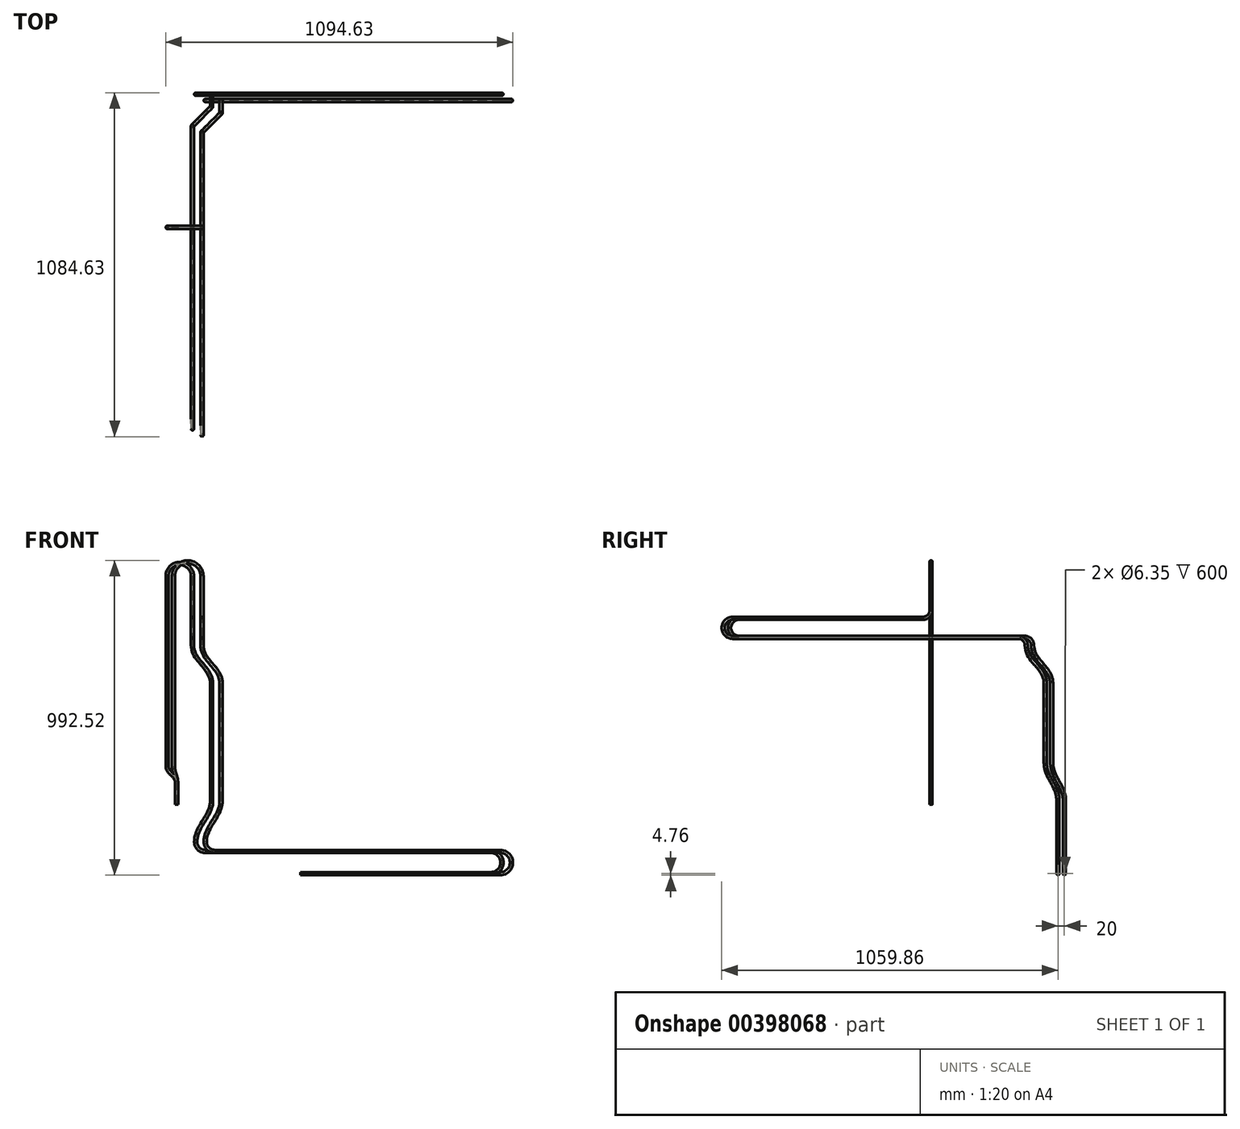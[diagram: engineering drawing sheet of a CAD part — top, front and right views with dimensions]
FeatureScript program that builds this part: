
annotation { "Feature Type Name" : "Feature", "Feature Type Description" : "" }
export const myFeature = defineFeature(function(context is Context, id is Id, definition is map)
    precondition{}
    {
        {
            var Q0;
            Q0=qCreatedBy(makeId("Top.planeOp"),FACE);
            var sketch = newSketch(context, id + "F0", { "sketchPlane" : qUnion([Q0])});
            skCircle(sketch, "E0", {"center": v(0, 0) * mm, "radius": 4.76 * mm});
            skCircle(sketch, "E1", {"center": v(0, 0) * mm, "radius": 3.17 * mm});
            skSolve(sketch);
        }
        {
            var Q0;
            Q0=qCreatedBy(makeId("Front.planeOp"),FACE);
            var sketch = newSketch(context, id + "F1", { "sketchPlane" : qUnion([Q0])});
            skLineSegment(sketch, "E2", {"start": v(80, 612) * mm, "end": v(80, 720) * mm});
            skArc(sketch, "E3", {"start": v(80, 720) * mm, "mid": v(35, 765) * mm, "end": v(-10, 720) * mm});
            skLineSegment(sketch, "E4", {"start": v(0, 70) * mm, "end": v(0, 0) * mm});
            skFitSpline(sketch, "E5", {"points": [v(0, 70) * mm, v(-5, 95) * mm, v(-10, 120) * mm], "startDerivative": vector(0, 60) * mm, "endDerivative": vector(0, 60) * mm});
            skLineSegment(sketch, "E6", {"start": v(-10, 110) * mm, "end": v(-10, 120) * mm, "construction": true});
            skLineSegment(sketch, "E7", {"start": v(0, 80) * mm, "end": v(0, 70) * mm, "construction": true});
            skLineSegment(sketch, "E8", {"start": v(0, 70) * mm, "end": v(-10, 120) * mm, "construction": true});
            skLineSegment(sketch, "E9", {"start": v(-10, 120) * mm, "end": v(-10, 720) * mm});
            skSolve(sketch);
        }
        {
            var Q0;
            Q0=qCreatedBy(makeId("Right.planeOp"),FACE);
            var Q1;
            Q1=sQuery(id+"F1.wireOp",VERTEX,"E2.start");
            cPlane(context, id + "F2", {"entities" : qUnion([Q0, Q1]), "cplaneType" : CPlaneType.PLANE_POINT, "offset" : 25 * mm, "width" : 150 * mm, "height" : 150 * mm});
        }
        {
            var Q0;
            Q0=qCreatedBy(id+"F2.planeOp",FACE);
            var sketch = newSketch(context, id + "F3", { "sketchPlane" : qUnion([Q0])});
            skArc(sketch, "E10.MirrorCS", {"start": v(0, 612) * mm, "mid": v(-7.32, 594.32) * mm, "end": v(-25, 587) * mm});
            skArc(sketch, "E11.MirrorCS", {"start": v(275, 527) * mm, "mid": v(292.68, 519.68) * mm, "end": v(300, 502) * mm});
            skLineSegment(sketch, "E12.MirrorCS", {"start": v(300, 502) * mm, "end": v(300, 517.1) * mm, "construction": true});
            skLineSegment(sketch, "E13.MirrorCS", {"start": v(-25, 587) * mm, "end": v(-625, 587) * mm});
            skArc(sketch, "E14.MirrorCS", {"start": v(-625, 527) * mm, "mid": v(-655, 557) * mm, "end": v(-625, 587) * mm});
            skLineSegment(sketch, "E15.MirrorCS", {"start": v(-625, 527) * mm, "end": v(275, 527) * mm});
            skSolve(sketch);
        }
        {
            var Q0;
            Q0=sQuery(id+"F3.wireOp",EDGE,"E12.MirrorCS");
            cPlane(context, id + "F4", {"entities" : qUnion([Q0]), "cplaneType" : CPlaneType.LINE_ANGLE, "offset" : 25 * mm, "angle" : 45 * degree, "oppositeDirection" : true, "width" : 150 * mm, "height" : 150 * mm});
        }
        {
            var Q0;
            Q0=qCreatedBy(id+"F4.planeOp",FACE);
            var sketch = newSketch(context, id + "F5", { "sketchPlane" : qUnion([Q0])});
            skFitSpline(sketch, "E16", {"points": [v(268.7, 502) * mm, v(311.2, 442) * mm, v(353.7, 382) * mm], "startDerivative": vector(0, -150) * mm, "endDerivative": vector(0, -150) * mm});
            skLineSegment(sketch, "E17", {"start": v(268.7, 477) * mm, "end": v(268.7, 502) * mm, "construction": true});
            skLineSegment(sketch, "E18", {"start": v(353.7, 407) * mm, "end": v(353.7, 382) * mm, "construction": true});
            skLineSegment(sketch, "E19", {"start": v(353.7, 382) * mm, "end": v(268.7, 502) * mm, "construction": true});
            skLineSegment(sketch, "E20", {"start": v(353.7, 382) * mm, "end": v(353.7, 132) * mm});
            skSolve(sketch);
        }
        {
            var Q0;
            Q0=qCreatedBy(makeId("Right.planeOp"),FACE);
            var Q1;
            Q1=sQuery(id+"F5.wireOp",VERTEX,"E20.end");
            cPlane(context, id + "F6", {"entities" : qUnion([Q0, Q1]), "cplaneType" : CPlaneType.PLANE_POINT, "offset" : 25 * mm, "width" : 150 * mm, "height" : 150 * mm});
        }
        {
            var Q0;
            Q0=qCreatedBy(id+"F6.planeOp",FACE);
            var sketch = newSketch(context, id + "F7", { "sketchPlane" : qUnion([Q0])});
            skFitSpline(sketch, "E21", {"points": [v(360.1, 132) * mm, v(380.1, 72) * mm, v(400.1, 12) * mm], "startDerivative": vector(0, -150) * mm, "endDerivative": vector(0, -150) * mm});
            skLineSegment(sketch, "E22", {"start": v(360.1, 132) * mm, "end": v(360.1, 107) * mm, "construction": true});
            skLineSegment(sketch, "E23", {"start": v(400.1, 37) * mm, "end": v(400.1, 12) * mm, "construction": true});
            skLineSegment(sketch, "E24", {"start": v(400.1, 12) * mm, "end": v(360.1, 132) * mm, "construction": true});
            skSolve(sketch);
        }
        {
            var Q0;
            Q0=sQuery(id+"F7.wireOp",VERTEX,"E21.end");
            var Q1;
            Q1=qCreatedBy(makeId("Front.planeOp"),FACE);
            cPlane(context, id + "F8", {"entities" : qUnion([Q0, Q1]), "cplaneType" : CPlaneType.PLANE_POINT, "offset" : 25 * mm, "width" : 150 * mm, "height" : 150 * mm});
        }
        {
            var Q0;
            Q0=qCreatedBy(id+"F8.planeOp",FACE);
            var sketch = newSketch(context, id + "F9", { "sketchPlane" : qUnion([Q0])});
            skFitSpline(sketch, "E25", {"points": [v(140.1, 12) * mm, v(115.1, -53) * mm, v(90.1, -118) * mm], "startDerivative": vector(0, -150) * mm, "endDerivative": vector(0, -150) * mm});
            skLineSegment(sketch, "E26", {"start": v(140.1, 12) * mm, "end": v(140.1, -13) * mm, "construction": true});
            skLineSegment(sketch, "E27", {"start": v(90.1, -93) * mm, "end": v(90.1, -118) * mm, "construction": true});
            skLineSegment(sketch, "E28", {"start": v(90.1, -118) * mm, "end": v(140.1, 12) * mm, "construction": true});
            skArc(sketch, "E29", {"start": v(90.1, -118) * mm, "mid": v(98.9, -139.21) * mm, "end": v(120.1, -148) * mm});
            skLineSegment(sketch, "E30", {"start": v(120.1, -148) * mm, "end": v(1020.1, -148) * mm});
            skArc(sketch, "E31", {"start": v(1020.1, -218) * mm, "mid": v(1055.1, -183) * mm, "end": v(1020.1, -148) * mm});
            skLineSegment(sketch, "E32", {"start": v(1020.1, -218) * mm, "end": v(420.1, -218) * mm});
            skSolve(sketch);
        }
        {
            var Q0;
            Q0=qSketchRegion(id+"F0",true);
            var Q1;
            Q1=qConstructionFilter(qBodyType(qCreatedBy(id+"F1",EDGE),BodyType.WIRE),ConstructionObject.NO);
            var Q2;
            Q2=qConstructionFilter(qBodyType(qCreatedBy(id+"F3",EDGE),BodyType.WIRE),ConstructionObject.NO);
            var Q3;
            Q3=qConstructionFilter(qBodyType(qCreatedBy(id+"F5",EDGE),BodyType.WIRE),ConstructionObject.NO);
            var Q4;
            Q4=qConstructionFilter(qBodyType(qCreatedBy(id+"F7",EDGE),BodyType.WIRE),ConstructionObject.NO);
            var Q5;
            Q5=qConstructionFilter(qBodyType(qCreatedBy(id+"F9",EDGE),BodyType.WIRE),ConstructionObject.NO);
            sweep(context, id + "F10", {"profiles" : qUnion([Q0]), "path" : qUnion([Q1, Q2, Q3, Q4, Q5])});
        }
        {
            var Q0;
            Q0=qCreatedBy(makeId("Front.planeOp"),FACE);
            var sketch = newSketch(context, id + "F11", { "sketchPlane" : qUnion([Q0])});
            skLineSegment(sketch, "E33", {"start": v(50, 612) * mm, "end": v(50, 720) * mm});
            skArc(sketch, "E34", {"start": v(50, 720) * mm, "mid": v(10, 760) * mm, "end": v(-30, 720) * mm});
            skLineSegment(sketch, "E35", {"start": v(0, 70) * mm, "end": v(0, 0) * mm});
            skFitSpline(sketch, "E36", {"points": [v(0, 70) * mm, v(-15, 95) * mm, v(-30, 120) * mm], "startDerivative": vector(0, 60) * mm, "endDerivative": vector(0, 60) * mm});
            skLineSegment(sketch, "E37", {"start": v(-30, 110) * mm, "end": v(-30, 120) * mm, "construction": true});
            skLineSegment(sketch, "E38", {"start": v(0, 80) * mm, "end": v(0, 70) * mm, "construction": true});
            skLineSegment(sketch, "E39", {"start": v(0, 70) * mm, "end": v(-30, 120) * mm, "construction": true});
            skLineSegment(sketch, "E40", {"start": v(-30, 120) * mm, "end": v(-30, 720) * mm});
            skSolve(sketch);
        }
        {
            var Q0;
            Q0=qCreatedBy(makeId("Right.planeOp"),FACE);
            var Q1;
            Q1=sQuery(id+"F11.wireOp",VERTEX,"E33.start");
            cPlane(context, id + "F12", {"entities" : qUnion([Q0, Q1]), "cplaneType" : CPlaneType.PLANE_POINT, "offset" : 25 * mm, "width" : 150 * mm, "height" : 150 * mm});
        }
        {
            var Q0;
            Q0=qCreatedBy(id+"F12.planeOp",FACE);
            var sketch = newSketch(context, id + "F13", { "sketchPlane" : qUnion([Q0])});
            skArc(sketch, "E41.MirrorCS", {"start": v(0, 612) * mm, "mid": v(-7.32, 594.32) * mm, "end": v(-25, 587) * mm});
            skArc(sketch, "E42.MirrorCS", {"start": v(295, 527) * mm, "mid": v(312.68, 519.68) * mm, "end": v(320, 502) * mm});
            skLineSegment(sketch, "E43.MirrorCS", {"start": v(320, 502) * mm, "end": v(320, 517.1) * mm, "construction": true});
            skLineSegment(sketch, "E44.MirrorCS", {"start": v(-25, 587) * mm, "end": v(-605, 587) * mm});
            skArc(sketch, "E45.MirrorCS", {"start": v(-605, 527) * mm, "mid": v(-635, 557) * mm, "end": v(-605, 587) * mm});
            skLineSegment(sketch, "E46.MirrorCS", {"start": v(-605, 527) * mm, "end": v(295, 527) * mm});
            skSolve(sketch);
        }
        {
            var Q0;
            Q0=sQuery(id+"F13.wireOp",EDGE,"E43.MirrorCS");
            cPlane(context, id + "F14", {"entities" : qUnion([Q0]), "cplaneType" : CPlaneType.LINE_ANGLE, "offset" : 25 * mm, "angle" : 45 * degree, "oppositeDirection" : true, "width" : 150 * mm, "height" : 150 * mm});
        }
        {
            var Q0;
            Q0=qCreatedBy(id+"F14.planeOp",FACE);
            var sketch = newSketch(context, id + "F15", { "sketchPlane" : qUnion([Q0])});
            skFitSpline(sketch, "E47", {"points": [v(261.63, 502) * mm, v(304.13, 442) * mm, v(346.63, 382) * mm], "startDerivative": vector(0, -150) * mm, "endDerivative": vector(0, -150) * mm});
            skLineSegment(sketch, "E48", {"start": v(261.63, 477) * mm, "end": v(261.63, 502) * mm, "construction": true});
            skLineSegment(sketch, "E49", {"start": v(346.63, 407) * mm, "end": v(346.63, 382) * mm, "construction": true});
            skLineSegment(sketch, "E50", {"start": v(346.63, 382) * mm, "end": v(261.63, 502) * mm, "construction": true});
            skLineSegment(sketch, "E51", {"start": v(346.63, 382) * mm, "end": v(346.63, 132) * mm});
            skSolve(sketch);
        }
        {
            var Q0;
            Q0=qCreatedBy(makeId("Right.planeOp"),FACE);
            var Q1;
            Q1=sQuery(id+"F15.wireOp",VERTEX,"E51.end");
            cPlane(context, id + "F16", {"entities" : qUnion([Q0, Q1]), "cplaneType" : CPlaneType.PLANE_POINT, "offset" : 25 * mm, "width" : 150 * mm, "height" : 150 * mm});
        }
        {
            var Q0;
            Q0=qCreatedBy(id+"F16.planeOp",FACE);
            var sketch = newSketch(context, id + "F17", { "sketchPlane" : qUnion([Q0])});
            skFitSpline(sketch, "E52", {"points": [v(380.1, 132) * mm, v(400.1, 72) * mm, v(420.1, 12) * mm], "startDerivative": vector(0, -150) * mm, "endDerivative": vector(0, -150) * mm});
            skLineSegment(sketch, "E53", {"start": v(380.1, 132) * mm, "end": v(380.1, 107) * mm, "construction": true});
            skLineSegment(sketch, "E54", {"start": v(420.1, 37) * mm, "end": v(420.1, 12) * mm, "construction": true});
            skLineSegment(sketch, "E55", {"start": v(420.1, 12) * mm, "end": v(380.1, 132) * mm, "construction": true});
            skSolve(sketch);
        }
        {
            var Q0;
            Q0=qCreatedBy(makeId("Front.planeOp"),FACE);
            var Q1;
            Q1=sQuery(id+"F17.wireOp",VERTEX,"E52.end");
            cPlane(context, id + "F18", {"entities" : qUnion([Q0, Q1]), "cplaneType" : CPlaneType.PLANE_POINT, "offset" : 25 * mm, "width" : 150 * mm, "height" : 150 * mm});
        }
        {
            var Q0;
            Q0=qCreatedBy(id+"F18.planeOp",FACE);
            var sketch = newSketch(context, id + "F19", { "sketchPlane" : qUnion([Q0])});
            skFitSpline(sketch, "E56", {"points": [v(110.1, 12) * mm, v(85.1, -53) * mm, v(60.1, -118) * mm], "startDerivative": vector(0, -150) * mm, "endDerivative": vector(0, -150) * mm});
            skLineSegment(sketch, "E57", {"start": v(110.1, 12) * mm, "end": v(110.1, -13) * mm, "construction": true});
            skLineSegment(sketch, "E58", {"start": v(60.1, -93) * mm, "end": v(60.1, -118) * mm, "construction": true});
            skLineSegment(sketch, "E59", {"start": v(60.1, -118) * mm, "end": v(110.1, 12) * mm, "construction": true});
            skArc(sketch, "E60", {"start": v(60.1, -118) * mm, "mid": v(68.9, -139.21) * mm, "end": v(90.1, -148) * mm});
            skLineSegment(sketch, "E61", {"start": v(90.1, -148) * mm, "end": v(990.1, -148) * mm});
            skArc(sketch, "E62", {"start": v(990.1, -218) * mm, "mid": v(1025.1, -183) * mm, "end": v(990.1, -148) * mm});
            skLineSegment(sketch, "E63", {"start": v(990.1, -218) * mm, "end": v(390.1, -218) * mm});
            skSolve(sketch);
        }
        {
            var Q0;
            Q0=qSketchRegion(id+"F0",true);
            var Q1;
            Q1=qConstructionFilter(qBodyType(qCreatedBy(id+"F11",EDGE),BodyType.WIRE),ConstructionObject.NO);
            var Q2;
            Q2=qConstructionFilter(qBodyType(qCreatedBy(id+"F13",EDGE),BodyType.WIRE),ConstructionObject.NO);
            var Q3;
            Q3=qConstructionFilter(qBodyType(qCreatedBy(id+"F15",EDGE),BodyType.WIRE),ConstructionObject.NO);
            var Q4;
            Q4=qConstructionFilter(qBodyType(qCreatedBy(id+"F17",EDGE),BodyType.WIRE),ConstructionObject.NO);
            var Q5;
            Q5=qConstructionFilter(qBodyType(qCreatedBy(id+"F19",EDGE),BodyType.WIRE),ConstructionObject.NO);
            sweep(context, id + "F20", {"profiles" : qUnion([Q0]), "path" : qUnion([Q1, Q2, Q3, Q4, Q5])});
        }
    });
